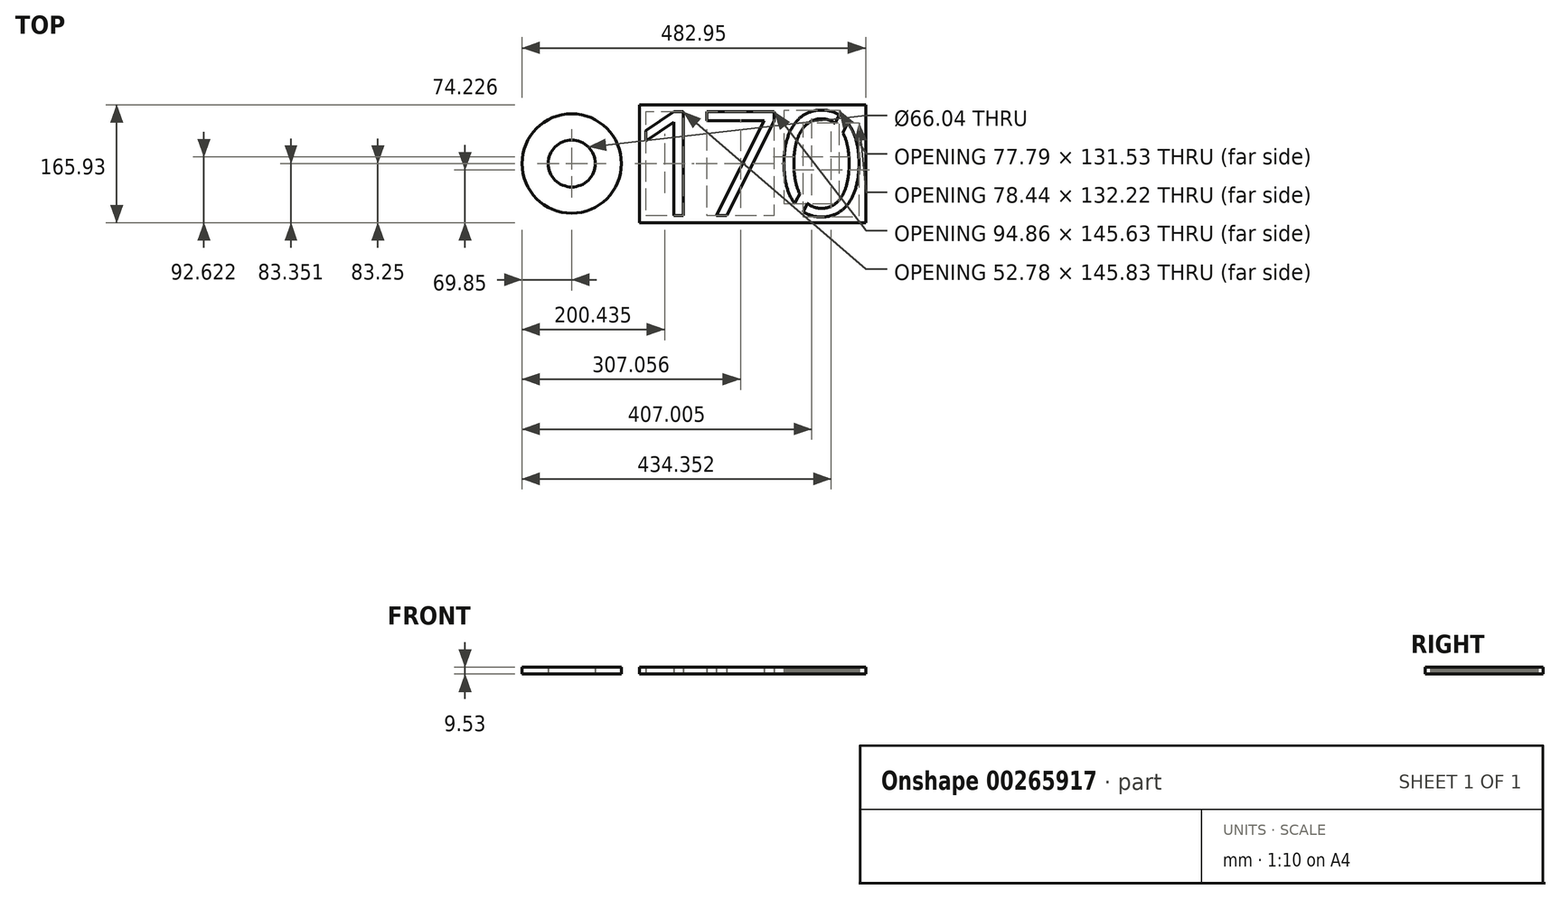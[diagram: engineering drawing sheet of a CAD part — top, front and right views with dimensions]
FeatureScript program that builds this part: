
annotation { "Feature Type Name" : "Feature", "Feature Type Description" : "" }
export const myFeature = defineFeature(function(context is Context, id is Id, definition is map)
    precondition{}
    {
        {
            var Q0;
            Q0=qCreatedBy(makeId("Top.planeOp"),FACE);
            var sketch = newSketch(context, id + "F0", { "sketchPlane" : qUnion([Q0])});
            skCircle(sketch, "E0", {"center": v(0, 0) * mm, "radius": 33.02 * mm});
            skCircle(sketch, "E1", {"center": v(0, 0) * mm, "radius": 69.85 * mm});
            skLineSegment(sketch, "E2", {"start": v(143.65, 58.18) * mm, "end": v(143.25, 58.18) * mm});
            skLineSegment(sketch, "E3", {"start": v(143.25, 58.18) * mm, "end": v(104.2, 31.34) * mm});
            skLineSegment(sketch, "E4", {"start": v(104.2, 31.34) * mm, "end": v(104.2, 46.07) * mm});
            skLineSegment(sketch, "E5", {"start": v(104.2, 46.07) * mm, "end": v(143.45, 73.02) * mm});
            skLineSegment(sketch, "E6", {"start": v(143.45, 73.02) * mm, "end": v(156.98, 73.02) * mm});
            skLineSegment(sketch, "E7", {"start": v(156.98, 73.02) * mm, "end": v(156.98, -72.81) * mm});
            skLineSegment(sketch, "E8", {"start": v(156.98, -72.81) * mm, "end": v(143.65, -72.81) * mm});
            skLineSegment(sketch, "E9", {"start": v(143.65, -72.81) * mm, "end": v(143.65, 58.18) * mm});
            skLineSegment(sketch, "E10", {"start": v(270.81, 60.1) * mm, "end": v(270.81, 60.5) * mm});
            skLineSegment(sketch, "E11", {"start": v(270.81, 60.5) * mm, "end": v(189.77, 60.5) * mm});
            skLineSegment(sketch, "E12", {"start": v(189.77, 60.5) * mm, "end": v(189.77, 72.81) * mm});
            skLineSegment(sketch, "E13", {"start": v(189.77, 72.81) * mm, "end": v(284.64, 72.81) * mm});
            skLineSegment(sketch, "E14", {"start": v(284.64, 72.81) * mm, "end": v(284.64, 59.9) * mm});
            skLineSegment(sketch, "E15", {"start": v(284.64, 59.9) * mm, "end": v(217.93, -72.81) * mm});
            skLineSegment(sketch, "E16", {"start": v(217.93, -72.81) * mm, "end": v(203.3, -72.81) * mm});
            skLineSegment(sketch, "E17", {"start": v(203.3, -72.81) * mm, "end": v(270.81, 60.1) * mm});
            skLineSegment(sketch, "E18", {"start": v(298.32, -4.21) * mm, "end": v(298.4, -6.3) * mm});
            skLineSegment(sketch, "E19", {"start": v(298.4, -6.3) * mm, "end": v(298.5, -8.38) * mm});
            skLineSegment(sketch, "E20", {"start": v(298.5, -8.38) * mm, "end": v(298.62, -10.42) * mm});
            skLineSegment(sketch, "E21", {"start": v(298.62, -10.42) * mm, "end": v(298.78, -12.44) * mm});
            skLineSegment(sketch, "E22", {"start": v(298.78, -12.44) * mm, "end": v(298.96, -14.43) * mm});
            skLineSegment(sketch, "E23", {"start": v(298.96, -14.43) * mm, "end": v(299.17, -16.4) * mm});
            skLineSegment(sketch, "E24", {"start": v(299.17, -16.4) * mm, "end": v(299.41, -18.33) * mm});
            skLineSegment(sketch, "E25", {"start": v(299.41, -18.33) * mm, "end": v(299.68, -20.24) * mm});
            skLineSegment(sketch, "E26", {"start": v(299.68, -20.24) * mm, "end": v(299.97, -22.12) * mm});
            skLineSegment(sketch, "E27", {"start": v(299.97, -22.12) * mm, "end": v(300.3, -23.98) * mm});
            skLineSegment(sketch, "E28", {"start": v(300.3, -23.98) * mm, "end": v(300.65, -25.8) * mm});
            skLineSegment(sketch, "E29", {"start": v(300.65, -25.8) * mm, "end": v(301.02, -27.6) * mm});
            skLineSegment(sketch, "E30", {"start": v(301.02, -27.6) * mm, "end": v(301.42, -29.37) * mm});
            skLineSegment(sketch, "E31", {"start": v(301.42, -29.37) * mm, "end": v(301.85, -31.11) * mm});
            skLineSegment(sketch, "E32", {"start": v(301.85, -31.11) * mm, "end": v(302.3, -32.82) * mm});
            skLineSegment(sketch, "E33", {"start": v(302.3, -32.82) * mm, "end": v(302.8, -34.5) * mm});
            skLineSegment(sketch, "E34", {"start": v(302.8, -34.5) * mm, "end": v(303.3, -36.16) * mm});
            skLineSegment(sketch, "E35", {"start": v(303.3, -36.16) * mm, "end": v(303.84, -37.78) * mm});
            skLineSegment(sketch, "E36", {"start": v(303.84, -37.78) * mm, "end": v(304.4, -39.37) * mm});
            skLineSegment(sketch, "E37", {"start": v(304.4, -39.37) * mm, "end": v(304.98, -40.93) * mm});
            skLineSegment(sketch, "E38", {"start": v(304.98, -40.93) * mm, "end": v(305.6, -42.46) * mm});
            skLineSegment(sketch, "E39", {"start": v(305.6, -42.46) * mm, "end": v(306.23, -43.96) * mm});
            skLineSegment(sketch, "E40", {"start": v(306.23, -43.96) * mm, "end": v(306.9, -45.43) * mm});
            skLineSegment(sketch, "E41", {"start": v(306.9, -45.43) * mm, "end": v(307.59, -46.87) * mm});
            skLineSegment(sketch, "E42", {"start": v(307.59, -46.87) * mm, "end": v(308.3, -48.27) * mm});
            skLineSegment(sketch, "E43", {"start": v(308.3, -48.27) * mm, "end": v(309.04, -49.64) * mm});
            skLineSegment(sketch, "E44", {"start": v(309.04, -49.64) * mm, "end": v(309.8, -50.98) * mm});
            skLineSegment(sketch, "E45", {"start": v(309.8, -50.98) * mm, "end": v(310.59, -52.29) * mm});
            skLineSegment(sketch, "E46", {"start": v(310.59, -52.29) * mm, "end": v(311.4, -53.56) * mm});
            skLineSegment(sketch, "E47", {"start": v(311.4, -53.56) * mm, "end": v(312.24, -54.8) * mm});
            skLineSegment(sketch, "E48", {"start": v(312.24, -54.8) * mm, "end": v(313.1, -56) * mm});
            skLineSegment(sketch, "E49", {"start": v(313.1, -56) * mm, "end": v(313.4, -56.4) * mm});
            skLineSegment(sketch, "E50", {"start": v(313.4, -56.4) * mm, "end": v(315.27, -52.65) * mm});
            skLineSegment(sketch, "E51", {"start": v(315.27, -52.65) * mm, "end": v(320.43, -42.4) * mm});
            skLineSegment(sketch, "E52", {"start": v(320.43, -42.4) * mm, "end": v(320.04, -41.6) * mm});
            skLineSegment(sketch, "E53", {"start": v(320.04, -41.6) * mm, "end": v(319.5, -40.44) * mm});
            skLineSegment(sketch, "E54", {"start": v(319.5, -40.44) * mm, "end": v(318.98, -39.26) * mm});
            skLineSegment(sketch, "E55", {"start": v(318.98, -39.26) * mm, "end": v(318.47, -38.06) * mm});
            skLineSegment(sketch, "E56", {"start": v(318.47, -38.06) * mm, "end": v(317.99, -36.82) * mm});
            skLineSegment(sketch, "E57", {"start": v(317.99, -36.82) * mm, "end": v(317.52, -35.56) * mm});
            skLineSegment(sketch, "E58", {"start": v(317.52, -35.56) * mm, "end": v(317.08, -34.28) * mm});
            skLineSegment(sketch, "E59", {"start": v(317.08, -34.28) * mm, "end": v(316.65, -32.97) * mm});
            skLineSegment(sketch, "E60", {"start": v(316.65, -32.97) * mm, "end": v(316.24, -31.63) * mm});
            skLineSegment(sketch, "E61", {"start": v(316.24, -31.63) * mm, "end": v(315.85, -30.27) * mm});
            skLineSegment(sketch, "E62", {"start": v(315.85, -30.27) * mm, "end": v(315.48, -28.88) * mm});
            skLineSegment(sketch, "E63", {"start": v(315.48, -28.88) * mm, "end": v(315.13, -27.46) * mm});
            skLineSegment(sketch, "E64", {"start": v(315.13, -27.46) * mm, "end": v(314.8, -26.03) * mm});
            skLineSegment(sketch, "E65", {"start": v(314.8, -26.03) * mm, "end": v(314.48, -24.56) * mm});
            skLineSegment(sketch, "E66", {"start": v(314.48, -24.56) * mm, "end": v(314.2, -23.08) * mm});
            skLineSegment(sketch, "E67", {"start": v(314.2, -23.08) * mm, "end": v(313.92, -21.57) * mm});
            skLineSegment(sketch, "E68", {"start": v(313.92, -21.57) * mm, "end": v(313.66, -20.03) * mm});
            skLineSegment(sketch, "E69", {"start": v(313.66, -20.03) * mm, "end": v(313.43, -18.47) * mm});
            skLineSegment(sketch, "E70", {"start": v(313.43, -18.47) * mm, "end": v(313.22, -16.9) * mm});
            skLineSegment(sketch, "E71", {"start": v(313.22, -16.9) * mm, "end": v(313.02, -15.29) * mm});
            skLineSegment(sketch, "E72", {"start": v(313.02, -15.29) * mm, "end": v(312.85, -13.66) * mm});
            skLineSegment(sketch, "E73", {"start": v(312.85, -13.66) * mm, "end": v(312.7, -12.01) * mm});
            skLineSegment(sketch, "E74", {"start": v(312.7, -12.01) * mm, "end": v(312.56, -10.34) * mm});
            skLineSegment(sketch, "E75", {"start": v(312.56, -10.34) * mm, "end": v(312.45, -8.64) * mm});
            skLineSegment(sketch, "E76", {"start": v(312.45, -8.64) * mm, "end": v(312.35, -6.93) * mm});
            skLineSegment(sketch, "E77", {"start": v(312.35, -6.93) * mm, "end": v(312.28, -5.19) * mm});
            skLineSegment(sketch, "E78", {"start": v(312.28, -5.19) * mm, "end": v(312.23, -3.43) * mm});
            skLineSegment(sketch, "E79", {"start": v(312.23, -3.43) * mm, "end": v(312.2, -1.65) * mm});
            skLineSegment(sketch, "E80", {"start": v(312.2, -1.65) * mm, "end": v(312.19, 0.15) * mm});
            skLineSegment(sketch, "E81", {"start": v(312.19, 0.15) * mm, "end": v(312.2, 1.92) * mm});
            skLineSegment(sketch, "E82", {"start": v(312.2, 1.92) * mm, "end": v(312.23, 3.67) * mm});
            skLineSegment(sketch, "E83", {"start": v(312.23, 3.67) * mm, "end": v(312.28, 5.4) * mm});
            skLineSegment(sketch, "E84", {"start": v(312.28, 5.4) * mm, "end": v(312.36, 7.1) * mm});
            skLineSegment(sketch, "E85", {"start": v(312.36, 7.1) * mm, "end": v(312.45, 8.8) * mm});
            skLineSegment(sketch, "E86", {"start": v(312.45, 8.8) * mm, "end": v(312.57, 10.47) * mm});
            skLineSegment(sketch, "E87", {"start": v(312.57, 10.47) * mm, "end": v(312.7, 12.12) * mm});
            skLineSegment(sketch, "E88", {"start": v(312.7, 12.12) * mm, "end": v(312.86, 13.74) * mm});
            skLineSegment(sketch, "E89", {"start": v(312.86, 13.74) * mm, "end": v(313.04, 15.35) * mm});
            skLineSegment(sketch, "E90", {"start": v(313.04, 15.35) * mm, "end": v(313.24, 16.93) * mm});
            skLineSegment(sketch, "E91", {"start": v(313.24, 16.93) * mm, "end": v(313.45, 18.5) * mm});
            skLineSegment(sketch, "E92", {"start": v(313.45, 18.5) * mm, "end": v(313.7, 20.04) * mm});
            skLineSegment(sketch, "E93", {"start": v(313.7, 20.04) * mm, "end": v(313.95, 21.55) * mm});
            skLineSegment(sketch, "E94", {"start": v(313.95, 21.55) * mm, "end": v(314.23, 23.05) * mm});
            skLineSegment(sketch, "E95", {"start": v(314.23, 23.05) * mm, "end": v(314.52, 24.52) * mm});
            skLineSegment(sketch, "E96", {"start": v(314.52, 24.52) * mm, "end": v(314.84, 25.97) * mm});
            skLineSegment(sketch, "E97", {"start": v(314.84, 25.97) * mm, "end": v(315.18, 27.4) * mm});
            skLineSegment(sketch, "E98", {"start": v(315.18, 27.4) * mm, "end": v(315.53, 28.8) * mm});
            skLineSegment(sketch, "E99", {"start": v(315.53, 28.8) * mm, "end": v(315.9, 30.17) * mm});
            skLineSegment(sketch, "E100", {"start": v(315.9, 30.17) * mm, "end": v(316.3, 31.52) * mm});
            skLineSegment(sketch, "E101", {"start": v(316.3, 31.52) * mm, "end": v(316.72, 32.85) * mm});
            skLineSegment(sketch, "E102", {"start": v(316.72, 32.85) * mm, "end": v(317.15, 34.16) * mm});
            skLineSegment(sketch, "E103", {"start": v(317.15, 34.16) * mm, "end": v(317.6, 35.44) * mm});
            skLineSegment(sketch, "E104", {"start": v(317.6, 35.44) * mm, "end": v(318.07, 36.69) * mm});
            skLineSegment(sketch, "E105", {"start": v(318.07, 36.69) * mm, "end": v(318.56, 37.92) * mm});
            skLineSegment(sketch, "E106", {"start": v(318.56, 37.92) * mm, "end": v(319.07, 39.12) * mm});
            skLineSegment(sketch, "E107", {"start": v(319.07, 39.12) * mm, "end": v(319.6, 40.3) * mm});
            skLineSegment(sketch, "E108", {"start": v(319.6, 40.3) * mm, "end": v(320.14, 41.44) * mm});
            skLineSegment(sketch, "E109", {"start": v(320.14, 41.44) * mm, "end": v(320.7, 42.56) * mm});
            skLineSegment(sketch, "E110", {"start": v(320.7, 42.56) * mm, "end": v(321.28, 43.66) * mm});
            skLineSegment(sketch, "E111", {"start": v(321.28, 43.66) * mm, "end": v(321.88, 44.73) * mm});
            skLineSegment(sketch, "E112", {"start": v(321.88, 44.73) * mm, "end": v(322.5, 45.77) * mm});
            skLineSegment(sketch, "E113", {"start": v(322.5, 45.77) * mm, "end": v(323.13, 46.78) * mm});
            skLineSegment(sketch, "E114", {"start": v(323.13, 46.78) * mm, "end": v(323.78, 47.76) * mm});
            skLineSegment(sketch, "E115", {"start": v(323.78, 47.76) * mm, "end": v(324.45, 48.72) * mm});
            skLineSegment(sketch, "E116", {"start": v(324.45, 48.72) * mm, "end": v(325.14, 49.65) * mm});
            skLineSegment(sketch, "E117", {"start": v(325.14, 49.65) * mm, "end": v(325.84, 50.55) * mm});
            skLineSegment(sketch, "E118", {"start": v(325.84, 50.55) * mm, "end": v(326.57, 51.42) * mm});
            skLineSegment(sketch, "E119", {"start": v(326.57, 51.42) * mm, "end": v(327.3, 52.26) * mm});
            skLineSegment(sketch, "E120", {"start": v(327.3, 52.26) * mm, "end": v(328.06, 53.07) * mm});
            skLineSegment(sketch, "E121", {"start": v(328.06, 53.07) * mm, "end": v(328.83, 53.85) * mm});
            skLineSegment(sketch, "E122", {"start": v(328.83, 53.85) * mm, "end": v(329.62, 54.6) * mm});
            skLineSegment(sketch, "E123", {"start": v(329.62, 54.6) * mm, "end": v(330.43, 55.32) * mm});
            skLineSegment(sketch, "E124", {"start": v(330.43, 55.32) * mm, "end": v(331.25, 56) * mm});
            skLineSegment(sketch, "E125", {"start": v(331.25, 56) * mm, "end": v(332.1, 56.67) * mm});
            skLineSegment(sketch, "E126", {"start": v(332.1, 56.67) * mm, "end": v(332.95, 57.3) * mm});
            skLineSegment(sketch, "E127", {"start": v(332.95, 57.3) * mm, "end": v(333.82, 57.89) * mm});
            skLineSegment(sketch, "E128", {"start": v(333.82, 57.89) * mm, "end": v(334.71, 58.45) * mm});
            skLineSegment(sketch, "E129", {"start": v(334.71, 58.45) * mm, "end": v(335.62, 58.98) * mm});
            skLineSegment(sketch, "E130", {"start": v(335.62, 58.98) * mm, "end": v(336.54, 59.48) * mm});
            skLineSegment(sketch, "E131", {"start": v(336.54, 59.48) * mm, "end": v(337.47, 59.95) * mm});
            skLineSegment(sketch, "E132", {"start": v(337.47, 59.95) * mm, "end": v(338.43, 60.38) * mm});
            skLineSegment(sketch, "E133", {"start": v(338.43, 60.38) * mm, "end": v(339.4, 60.78) * mm});
            skLineSegment(sketch, "E134", {"start": v(339.4, 60.78) * mm, "end": v(340.38, 61.15) * mm});
            skLineSegment(sketch, "E135", {"start": v(340.38, 61.15) * mm, "end": v(341.38, 61.48) * mm});
            skLineSegment(sketch, "E136", {"start": v(341.38, 61.48) * mm, "end": v(342.4, 61.78) * mm});
            skLineSegment(sketch, "E137", {"start": v(342.4, 61.78) * mm, "end": v(343.42, 62.05) * mm});
            skLineSegment(sketch, "E138", {"start": v(343.42, 62.05) * mm, "end": v(344.46, 62.28) * mm});
            skLineSegment(sketch, "E139", {"start": v(344.46, 62.28) * mm, "end": v(345.52, 62.47) * mm});
            skLineSegment(sketch, "E140", {"start": v(345.52, 62.47) * mm, "end": v(346.6, 62.64) * mm});
            skLineSegment(sketch, "E141", {"start": v(346.6, 62.64) * mm, "end": v(347.69, 62.76) * mm});
            skLineSegment(sketch, "E142", {"start": v(347.69, 62.76) * mm, "end": v(348.8, 62.85) * mm});
            skLineSegment(sketch, "E143", {"start": v(348.8, 62.85) * mm, "end": v(349.91, 62.9) * mm});
            skLineSegment(sketch, "E144", {"start": v(349.91, 62.9) * mm, "end": v(351.04, 62.92) * mm});
            skLineSegment(sketch, "E145", {"start": v(351.04, 62.92) * mm, "end": v(352.18, 62.9) * mm});
            skLineSegment(sketch, "E146", {"start": v(352.18, 62.9) * mm, "end": v(353.3, 62.85) * mm});
            skLineSegment(sketch, "E147", {"start": v(353.3, 62.85) * mm, "end": v(354.41, 62.76) * mm});
            skLineSegment(sketch, "E148", {"start": v(354.41, 62.76) * mm, "end": v(355.5, 62.64) * mm});
            skLineSegment(sketch, "E149", {"start": v(355.5, 62.64) * mm, "end": v(356.58, 62.48) * mm});
            skLineSegment(sketch, "E150", {"start": v(356.58, 62.48) * mm, "end": v(357.64, 62.28) * mm});
            skLineSegment(sketch, "E151", {"start": v(357.64, 62.28) * mm, "end": v(358.7, 62.05) * mm});
            skLineSegment(sketch, "E152", {"start": v(358.7, 62.05) * mm, "end": v(359.72, 61.8) * mm});
            skLineSegment(sketch, "E153", {"start": v(359.72, 61.8) * mm, "end": v(360.74, 61.5) * mm});
            skLineSegment(sketch, "E154", {"start": v(360.74, 61.5) * mm, "end": v(361.74, 61.16) * mm});
            skLineSegment(sketch, "E155", {"start": v(361.74, 61.16) * mm, "end": v(362.73, 60.8) * mm});
            skLineSegment(sketch, "E156", {"start": v(362.73, 60.8) * mm, "end": v(363.7, 60.4) * mm});
            skLineSegment(sketch, "E157", {"start": v(363.7, 60.4) * mm, "end": v(364.65, 59.97) * mm});
            skLineSegment(sketch, "E158", {"start": v(364.65, 59.97) * mm, "end": v(365.59, 59.5) * mm});
            skLineSegment(sketch, "E159", {"start": v(365.59, 59.5) * mm, "end": v(366.51, 59) * mm});
            skLineSegment(sketch, "E160", {"start": v(366.51, 59) * mm, "end": v(367.42, 58.48) * mm});
            skLineSegment(sketch, "E161", {"start": v(367.42, 58.48) * mm, "end": v(368.3, 57.92) * mm});
            skLineSegment(sketch, "E162", {"start": v(368.3, 57.92) * mm, "end": v(369.18, 57.32) * mm});
            skLineSegment(sketch, "E163", {"start": v(369.18, 57.32) * mm, "end": v(370.04, 56.7) * mm});
            skLineSegment(sketch, "E164", {"start": v(370.04, 56.7) * mm, "end": v(370.2, 56.57) * mm});
            skLineSegment(sketch, "E165", {"start": v(370.2, 56.57) * mm, "end": v(372, 60.15) * mm});
            skLineSegment(sketch, "E166", {"start": v(372, 60.15) * mm, "end": v(376.05, 68.18) * mm});
            skLineSegment(sketch, "E167", {"start": v(376.05, 68.18) * mm, "end": v(375.58, 68.47) * mm});
            skLineSegment(sketch, "E168", {"start": v(375.58, 68.47) * mm, "end": v(374.4, 69.18) * mm});
            skLineSegment(sketch, "E169", {"start": v(374.4, 69.18) * mm, "end": v(373.2, 69.85) * mm});
            skLineSegment(sketch, "E170", {"start": v(373.2, 69.85) * mm, "end": v(371.97, 70.48) * mm});
            skLineSegment(sketch, "E171", {"start": v(371.97, 70.48) * mm, "end": v(370.72, 71.07) * mm});
            skLineSegment(sketch, "E172", {"start": v(370.72, 71.07) * mm, "end": v(369.45, 71.62) * mm});
            skLineSegment(sketch, "E173", {"start": v(369.45, 71.62) * mm, "end": v(368.16, 72.13) * mm});
            skLineSegment(sketch, "E174", {"start": v(368.16, 72.13) * mm, "end": v(366.85, 72.6) * mm});
            skLineSegment(sketch, "E175", {"start": v(366.85, 72.6) * mm, "end": v(365.51, 73.04) * mm});
            skLineSegment(sketch, "E176", {"start": v(365.51, 73.04) * mm, "end": v(364.16, 73.43) * mm});
            skLineSegment(sketch, "E177", {"start": v(364.16, 73.43) * mm, "end": v(362.78, 73.79) * mm});
            skLineSegment(sketch, "E178", {"start": v(362.78, 73.79) * mm, "end": v(361.38, 74.1) * mm});
            skLineSegment(sketch, "E179", {"start": v(361.38, 74.1) * mm, "end": v(359.97, 74.37) * mm});
            skLineSegment(sketch, "E180", {"start": v(359.97, 74.37) * mm, "end": v(358.53, 74.6) * mm});
            skLineSegment(sketch, "E181", {"start": v(358.53, 74.6) * mm, "end": v(357.07, 74.8) * mm});
            skLineSegment(sketch, "E182", {"start": v(357.07, 74.8) * mm, "end": v(355.6, 74.94) * mm});
            skLineSegment(sketch, "E183", {"start": v(355.6, 74.94) * mm, "end": v(354.1, 75.05) * mm});
            skLineSegment(sketch, "E184", {"start": v(354.1, 75.05) * mm, "end": v(352.58, 75.11) * mm});
            skLineSegment(sketch, "E185", {"start": v(352.58, 75.11) * mm, "end": v(351.04, 75.13) * mm});
            skLineSegment(sketch, "E186", {"start": v(351.04, 75.13) * mm, "end": v(349.51, 75.11) * mm});
            skLineSegment(sketch, "E187", {"start": v(349.51, 75.11) * mm, "end": v(348, 75.05) * mm});
            skLineSegment(sketch, "E188", {"start": v(348, 75.05) * mm, "end": v(346.5, 74.94) * mm});
            skLineSegment(sketch, "E189", {"start": v(346.5, 74.94) * mm, "end": v(345.03, 74.8) * mm});
            skLineSegment(sketch, "E190", {"start": v(345.03, 74.8) * mm, "end": v(343.57, 74.6) * mm});
            skLineSegment(sketch, "E191", {"start": v(343.57, 74.6) * mm, "end": v(342.14, 74.37) * mm});
            skLineSegment(sketch, "E192", {"start": v(342.14, 74.37) * mm, "end": v(340.72, 74.1) * mm});
            skLineSegment(sketch, "E193", {"start": v(340.72, 74.1) * mm, "end": v(339.33, 73.78) * mm});
            skLineSegment(sketch, "E194", {"start": v(339.33, 73.78) * mm, "end": v(337.95, 73.43) * mm});
            skLineSegment(sketch, "E195", {"start": v(337.95, 73.43) * mm, "end": v(336.6, 73.03) * mm});
            skLineSegment(sketch, "E196", {"start": v(336.6, 73.03) * mm, "end": v(335.27, 72.6) * mm});
            skLineSegment(sketch, "E197", {"start": v(335.27, 72.6) * mm, "end": v(333.96, 72.12) * mm});
            skLineSegment(sketch, "E198", {"start": v(333.96, 72.12) * mm, "end": v(332.66, 71.6) * mm});
            skLineSegment(sketch, "E199", {"start": v(332.66, 71.6) * mm, "end": v(331.4, 71.06) * mm});
            skLineSegment(sketch, "E200", {"start": v(331.4, 71.06) * mm, "end": v(330.14, 70.46) * mm});
            skLineSegment(sketch, "E201", {"start": v(330.14, 70.46) * mm, "end": v(328.92, 69.83) * mm});
            skLineSegment(sketch, "E202", {"start": v(328.92, 69.83) * mm, "end": v(327.71, 69.16) * mm});
            skLineSegment(sketch, "E203", {"start": v(327.71, 69.16) * mm, "end": v(326.53, 68.46) * mm});
            skLineSegment(sketch, "E204", {"start": v(326.53, 68.46) * mm, "end": v(325.36, 67.71) * mm});
            skLineSegment(sketch, "E205", {"start": v(325.36, 67.71) * mm, "end": v(324.22, 66.93) * mm});
            skLineSegment(sketch, "E206", {"start": v(324.22, 66.93) * mm, "end": v(323.1, 66.1) * mm});
            skLineSegment(sketch, "E207", {"start": v(323.1, 66.1) * mm, "end": v(322, 65.25) * mm});
            skLineSegment(sketch, "E208", {"start": v(322, 65.25) * mm, "end": v(320.94, 64.36) * mm});
            skLineSegment(sketch, "E209", {"start": v(320.94, 64.36) * mm, "end": v(319.88, 63.43) * mm});
            skLineSegment(sketch, "E210", {"start": v(319.88, 63.43) * mm, "end": v(318.86, 62.47) * mm});
            skLineSegment(sketch, "E211", {"start": v(318.86, 62.47) * mm, "end": v(317.85, 61.47) * mm});
            skLineSegment(sketch, "E212", {"start": v(317.85, 61.47) * mm, "end": v(316.87, 60.43) * mm});
            skLineSegment(sketch, "E213", {"start": v(316.87, 60.43) * mm, "end": v(315.91, 59.36) * mm});
            skLineSegment(sketch, "E214", {"start": v(315.91, 59.36) * mm, "end": v(314.98, 58.26) * mm});
            skLineSegment(sketch, "E215", {"start": v(314.98, 58.26) * mm, "end": v(314.07, 57.12) * mm});
            skLineSegment(sketch, "E216", {"start": v(314.07, 57.12) * mm, "end": v(313.18, 55.94) * mm});
            skLineSegment(sketch, "E217", {"start": v(313.18, 55.94) * mm, "end": v(312.31, 54.74) * mm});
            skLineSegment(sketch, "E218", {"start": v(312.31, 54.74) * mm, "end": v(311.48, 53.5) * mm});
            skLineSegment(sketch, "E219", {"start": v(311.48, 53.5) * mm, "end": v(310.66, 52.22) * mm});
            skLineSegment(sketch, "E220", {"start": v(310.66, 52.22) * mm, "end": v(309.87, 50.91) * mm});
            skLineSegment(sketch, "E221", {"start": v(309.87, 50.91) * mm, "end": v(309.1, 49.58) * mm});
            skLineSegment(sketch, "E222", {"start": v(309.1, 49.58) * mm, "end": v(308.36, 48.2) * mm});
            skLineSegment(sketch, "E223", {"start": v(308.36, 48.2) * mm, "end": v(307.65, 46.8) * mm});
            skLineSegment(sketch, "E224", {"start": v(307.65, 46.8) * mm, "end": v(306.95, 45.36) * mm});
            skLineSegment(sketch, "E225", {"start": v(306.95, 45.36) * mm, "end": v(306.29, 43.9) * mm});
            skLineSegment(sketch, "E226", {"start": v(306.29, 43.9) * mm, "end": v(305.65, 42.4) * mm});
            skLineSegment(sketch, "E227", {"start": v(305.65, 42.4) * mm, "end": v(305.03, 40.87) * mm});
            skLineSegment(sketch, "E228", {"start": v(305.03, 40.87) * mm, "end": v(304.44, 39.31) * mm});
            skLineSegment(sketch, "E229", {"start": v(304.44, 39.31) * mm, "end": v(303.88, 37.72) * mm});
            skLineSegment(sketch, "E230", {"start": v(303.88, 37.72) * mm, "end": v(303.34, 36.1) * mm});
            skLineSegment(sketch, "E231", {"start": v(303.34, 36.1) * mm, "end": v(302.83, 34.45) * mm});
            skLineSegment(sketch, "E232", {"start": v(302.83, 34.45) * mm, "end": v(302.34, 32.78) * mm});
            skLineSegment(sketch, "E233", {"start": v(302.34, 32.78) * mm, "end": v(301.88, 31.07) * mm});
            skLineSegment(sketch, "E234", {"start": v(301.88, 31.07) * mm, "end": v(301.45, 29.33) * mm});
            skLineSegment(sketch, "E235", {"start": v(301.45, 29.33) * mm, "end": v(301.04, 27.57) * mm});
            skLineSegment(sketch, "E236", {"start": v(301.04, 27.57) * mm, "end": v(300.67, 25.78) * mm});
            skLineSegment(sketch, "E237", {"start": v(300.67, 25.78) * mm, "end": v(300.31, 23.96) * mm});
            skLineSegment(sketch, "E238", {"start": v(300.31, 23.96) * mm, "end": v(299.99, 22.1) * mm});
            skLineSegment(sketch, "E239", {"start": v(299.99, 22.1) * mm, "end": v(299.7, 20.23) * mm});
            skLineSegment(sketch, "E240", {"start": v(299.7, 20.23) * mm, "end": v(299.42, 18.33) * mm});
            skLineSegment(sketch, "E241", {"start": v(299.42, 18.33) * mm, "end": v(299.18, 16.4) * mm});
            skLineSegment(sketch, "E242", {"start": v(299.18, 16.4) * mm, "end": v(298.97, 14.45) * mm});
            skLineSegment(sketch, "E243", {"start": v(298.97, 14.45) * mm, "end": v(298.78, 12.47) * mm});
            skLineSegment(sketch, "E244", {"start": v(298.78, 12.47) * mm, "end": v(298.62, 10.46) * mm});
            skLineSegment(sketch, "E245", {"start": v(298.62, 10.46) * mm, "end": v(298.5, 8.43) * mm});
            skLineSegment(sketch, "E246", {"start": v(298.5, 8.43) * mm, "end": v(298.4, 6.37) * mm});
            skLineSegment(sketch, "E247", {"start": v(298.4, 6.37) * mm, "end": v(298.32, 4.29) * mm});
            skLineSegment(sketch, "E248", {"start": v(298.32, 4.29) * mm, "end": v(298.28, 2.18) * mm});
            skLineSegment(sketch, "E249", {"start": v(298.28, 2.18) * mm, "end": v(298.26, 0.05) * mm});
            skLineSegment(sketch, "E250", {"start": v(298.26, 0.05) * mm, "end": v(298.28, -2.1) * mm});
            skLineSegment(sketch, "E251", {"start": v(298.28, -2.1) * mm, "end": v(298.32, -4.21) * mm});
            skLineSegment(sketch, "E252", {"start": v(403.67, 4.39) * mm, "end": v(403.6, 6.47) * mm});
            skLineSegment(sketch, "E253", {"start": v(403.6, 6.47) * mm, "end": v(403.5, 8.53) * mm});
            skLineSegment(sketch, "E254", {"start": v(403.5, 8.53) * mm, "end": v(403.37, 10.56) * mm});
            skLineSegment(sketch, "E255", {"start": v(403.37, 10.56) * mm, "end": v(403.2, 12.56) * mm});
            skLineSegment(sketch, "E256", {"start": v(403.2, 12.56) * mm, "end": v(403.03, 14.55) * mm});
            skLineSegment(sketch, "E257", {"start": v(403.03, 14.55) * mm, "end": v(402.81, 16.5) * mm});
            skLineSegment(sketch, "E258", {"start": v(402.81, 16.5) * mm, "end": v(402.57, 18.43) * mm});
            skLineSegment(sketch, "E259", {"start": v(402.57, 18.43) * mm, "end": v(402.3, 20.33) * mm});
            skLineSegment(sketch, "E260", {"start": v(402.3, 20.33) * mm, "end": v(402.01, 22.2) * mm});
            skLineSegment(sketch, "E261", {"start": v(402.01, 22.2) * mm, "end": v(401.69, 24.05) * mm});
            skLineSegment(sketch, "E262", {"start": v(401.69, 24.05) * mm, "end": v(401.34, 25.87) * mm});
            skLineSegment(sketch, "E263", {"start": v(401.34, 25.87) * mm, "end": v(400.96, 27.66) * mm});
            skLineSegment(sketch, "E264", {"start": v(400.96, 27.66) * mm, "end": v(400.56, 29.42) * mm});
            skLineSegment(sketch, "E265", {"start": v(400.56, 29.42) * mm, "end": v(400.13, 31.15) * mm});
            skLineSegment(sketch, "E266", {"start": v(400.13, 31.15) * mm, "end": v(399.68, 32.86) * mm});
            skLineSegment(sketch, "E267", {"start": v(399.68, 32.86) * mm, "end": v(399.2, 34.54) * mm});
            skLineSegment(sketch, "E268", {"start": v(399.2, 34.54) * mm, "end": v(398.69, 36.18) * mm});
            skLineSegment(sketch, "E269", {"start": v(398.69, 36.18) * mm, "end": v(398.15, 37.8) * mm});
            skLineSegment(sketch, "E270", {"start": v(398.15, 37.8) * mm, "end": v(397.6, 39.39) * mm});
            skLineSegment(sketch, "E271", {"start": v(397.6, 39.39) * mm, "end": v(397, 40.94) * mm});
            skLineSegment(sketch, "E272", {"start": v(397, 40.94) * mm, "end": v(396.4, 42.47) * mm});
            skLineSegment(sketch, "E273", {"start": v(396.4, 42.47) * mm, "end": v(395.76, 43.97) * mm});
            skLineSegment(sketch, "E274", {"start": v(395.76, 43.97) * mm, "end": v(395.1, 45.43) * mm});
            skLineSegment(sketch, "E275", {"start": v(395.1, 45.43) * mm, "end": v(394.4, 46.86) * mm});
            skLineSegment(sketch, "E276", {"start": v(394.4, 46.86) * mm, "end": v(393.7, 48.27) * mm});
            skLineSegment(sketch, "E277", {"start": v(393.7, 48.27) * mm, "end": v(392.96, 49.64) * mm});
            skLineSegment(sketch, "E278", {"start": v(392.96, 49.64) * mm, "end": v(392.2, 50.97) * mm});
            skLineSegment(sketch, "E279", {"start": v(392.2, 50.97) * mm, "end": v(391.4, 52.28) * mm});
            skLineSegment(sketch, "E280", {"start": v(391.4, 52.28) * mm, "end": v(390.6, 53.55) * mm});
            skLineSegment(sketch, "E281", {"start": v(390.6, 53.55) * mm, "end": v(389.76, 54.79) * mm});
            skLineSegment(sketch, "E282", {"start": v(389.76, 54.79) * mm, "end": v(388.9, 56) * mm});
            skLineSegment(sketch, "E283", {"start": v(388.9, 56) * mm, "end": v(388.07, 57.09) * mm});
            skLineSegment(sketch, "E284", {"start": v(388.07, 57.09) * mm, "end": v(386.06, 53.08) * mm});
            skLineSegment(sketch, "E285", {"start": v(386.06, 53.08) * mm, "end": v(381.1, 43.23) * mm});
            skLineSegment(sketch, "E286", {"start": v(381.1, 43.23) * mm, "end": v(381.42, 42.63) * mm});
            skLineSegment(sketch, "E287", {"start": v(381.42, 42.63) * mm, "end": v(381.98, 41.5) * mm});
            skLineSegment(sketch, "E288", {"start": v(381.98, 41.5) * mm, "end": v(382.53, 40.36) * mm});
            skLineSegment(sketch, "E289", {"start": v(382.53, 40.36) * mm, "end": v(383.05, 39.18) * mm});
            skLineSegment(sketch, "E290", {"start": v(383.05, 39.18) * mm, "end": v(383.56, 37.98) * mm});
            skLineSegment(sketch, "E291", {"start": v(383.56, 37.98) * mm, "end": v(384.04, 36.75) * mm});
            skLineSegment(sketch, "E292", {"start": v(384.04, 36.75) * mm, "end": v(384.51, 35.5) * mm});
            skLineSegment(sketch, "E293", {"start": v(384.51, 35.5) * mm, "end": v(384.96, 34.22) * mm});
            skLineSegment(sketch, "E294", {"start": v(384.96, 34.22) * mm, "end": v(385.4, 32.91) * mm});
            skLineSegment(sketch, "E295", {"start": v(385.4, 32.91) * mm, "end": v(385.8, 31.58) * mm});
            skLineSegment(sketch, "E296", {"start": v(385.8, 31.58) * mm, "end": v(386.2, 30.23) * mm});
            skLineSegment(sketch, "E297", {"start": v(386.2, 30.23) * mm, "end": v(386.57, 28.84) * mm});
            skLineSegment(sketch, "E298", {"start": v(386.57, 28.84) * mm, "end": v(386.93, 27.44) * mm});
            skLineSegment(sketch, "E299", {"start": v(386.93, 27.44) * mm, "end": v(387.26, 26.01) * mm});
            skLineSegment(sketch, "E300", {"start": v(387.26, 26.01) * mm, "end": v(387.58, 24.56) * mm});
            skLineSegment(sketch, "E301", {"start": v(387.58, 24.56) * mm, "end": v(387.87, 23.08) * mm});
            skLineSegment(sketch, "E302", {"start": v(387.87, 23.08) * mm, "end": v(388.15, 21.58) * mm});
            skLineSegment(sketch, "E303", {"start": v(388.15, 21.58) * mm, "end": v(388.4, 20.06) * mm});
            skLineSegment(sketch, "E304", {"start": v(388.4, 20.06) * mm, "end": v(388.64, 18.5) * mm});
            skLineSegment(sketch, "E305", {"start": v(388.64, 18.5) * mm, "end": v(388.86, 16.94) * mm});
            skLineSegment(sketch, "E306", {"start": v(388.86, 16.94) * mm, "end": v(389.05, 15.35) * mm});
            skLineSegment(sketch, "E307", {"start": v(389.05, 15.35) * mm, "end": v(389.23, 13.73) * mm});
            skLineSegment(sketch, "E308", {"start": v(389.23, 13.73) * mm, "end": v(389.39, 12.1) * mm});
            skLineSegment(sketch, "E309", {"start": v(389.39, 12.1) * mm, "end": v(389.52, 10.44) * mm});
            skLineSegment(sketch, "E310", {"start": v(389.52, 10.44) * mm, "end": v(389.64, 8.76) * mm});
            skLineSegment(sketch, "E311", {"start": v(389.64, 8.76) * mm, "end": v(389.73, 7.06) * mm});
            skLineSegment(sketch, "E312", {"start": v(389.73, 7.06) * mm, "end": v(389.8, 5.34) * mm});
            skLineSegment(sketch, "E313", {"start": v(389.8, 5.34) * mm, "end": v(389.85, 3.6) * mm});
            skLineSegment(sketch, "E314", {"start": v(389.85, 3.6) * mm, "end": v(389.89, 1.83) * mm});
            skLineSegment(sketch, "E315", {"start": v(389.89, 1.83) * mm, "end": v(389.9, 0.05) * mm});
            skLineSegment(sketch, "E316", {"start": v(389.9, 0.05) * mm, "end": v(389.89, -1.75) * mm});
            skLineSegment(sketch, "E317", {"start": v(389.89, -1.75) * mm, "end": v(389.86, -3.52) * mm});
            skLineSegment(sketch, "E318", {"start": v(389.86, -3.52) * mm, "end": v(389.8, -5.28) * mm});
            skLineSegment(sketch, "E319", {"start": v(389.8, -5.28) * mm, "end": v(389.73, -7.01) * mm});
            skLineSegment(sketch, "E320", {"start": v(389.73, -7.01) * mm, "end": v(389.64, -8.72) * mm});
            skLineSegment(sketch, "E321", {"start": v(389.64, -8.72) * mm, "end": v(389.53, -10.41) * mm});
            skLineSegment(sketch, "E322", {"start": v(389.53, -10.41) * mm, "end": v(389.4, -12.08) * mm});
            skLineSegment(sketch, "E323", {"start": v(389.4, -12.08) * mm, "end": v(389.24, -13.73) * mm});
            skLineSegment(sketch, "E324", {"start": v(389.24, -13.73) * mm, "end": v(389.06, -15.35) * mm});
            skLineSegment(sketch, "E325", {"start": v(389.06, -15.35) * mm, "end": v(388.87, -16.95) * mm});
            skLineSegment(sketch, "E326", {"start": v(388.87, -16.95) * mm, "end": v(388.66, -18.53) * mm});
            skLineSegment(sketch, "E327", {"start": v(388.66, -18.53) * mm, "end": v(388.42, -20.09) * mm});
            skLineSegment(sketch, "E328", {"start": v(388.42, -20.09) * mm, "end": v(388.17, -21.62) * mm});
            skLineSegment(sketch, "E329", {"start": v(388.17, -21.62) * mm, "end": v(387.9, -23.13) * mm});
            skLineSegment(sketch, "E330", {"start": v(387.9, -23.13) * mm, "end": v(387.6, -24.6) * mm});
            skLineSegment(sketch, "E331", {"start": v(387.6, -24.6) * mm, "end": v(387.29, -26.07) * mm});
            skLineSegment(sketch, "E332", {"start": v(387.29, -26.07) * mm, "end": v(386.96, -27.5) * mm});
            skLineSegment(sketch, "E333", {"start": v(386.96, -27.5) * mm, "end": v(386.6, -28.91) * mm});
            skLineSegment(sketch, "E334", {"start": v(386.6, -28.91) * mm, "end": v(386.24, -30.3) * mm});
            skLineSegment(sketch, "E335", {"start": v(386.24, -30.3) * mm, "end": v(385.85, -31.66) * mm});
            skLineSegment(sketch, "E336", {"start": v(385.85, -31.66) * mm, "end": v(385.44, -33) * mm});
            skLineSegment(sketch, "E337", {"start": v(385.44, -33) * mm, "end": v(385, -34.3) * mm});
            skLineSegment(sketch, "E338", {"start": v(385, -34.3) * mm, "end": v(384.56, -35.6) * mm});
            skLineSegment(sketch, "E339", {"start": v(384.56, -35.6) * mm, "end": v(384.1, -36.85) * mm});
            skLineSegment(sketch, "E340", {"start": v(384.1, -36.85) * mm, "end": v(383.61, -38.08) * mm});
            skLineSegment(sketch, "E341", {"start": v(383.61, -38.08) * mm, "end": v(383.1, -39.28) * mm});
            skLineSegment(sketch, "E342", {"start": v(383.1, -39.28) * mm, "end": v(382.59, -40.46) * mm});
            skLineSegment(sketch, "E343", {"start": v(382.59, -40.46) * mm, "end": v(382.05, -41.61) * mm});
            skLineSegment(sketch, "E344", {"start": v(382.05, -41.61) * mm, "end": v(381.49, -42.74) * mm});
            skLineSegment(sketch, "E345", {"start": v(381.49, -42.74) * mm, "end": v(380.91, -43.83) * mm});
            skLineSegment(sketch, "E346", {"start": v(380.91, -43.83) * mm, "end": v(380.32, -44.9) * mm});
            skLineSegment(sketch, "E347", {"start": v(380.32, -44.9) * mm, "end": v(379.7, -45.94) * mm});
            skLineSegment(sketch, "E348", {"start": v(379.7, -45.94) * mm, "end": v(379.07, -46.96) * mm});
            skLineSegment(sketch, "E349", {"start": v(379.07, -46.96) * mm, "end": v(378.42, -47.94) * mm});
            skLineSegment(sketch, "E350", {"start": v(378.42, -47.94) * mm, "end": v(377.76, -48.9) * mm});
            skLineSegment(sketch, "E351", {"start": v(377.76, -48.9) * mm, "end": v(377.07, -49.82) * mm});
            skLineSegment(sketch, "E352", {"start": v(377.07, -49.82) * mm, "end": v(376.37, -50.72) * mm});
            skLineSegment(sketch, "E353", {"start": v(376.37, -50.72) * mm, "end": v(375.65, -51.59) * mm});
            skLineSegment(sketch, "E354", {"start": v(375.65, -51.59) * mm, "end": v(374.91, -52.42) * mm});
            skLineSegment(sketch, "E355", {"start": v(374.91, -52.42) * mm, "end": v(374.16, -53.23) * mm});
            skLineSegment(sketch, "E356", {"start": v(374.16, -53.23) * mm, "end": v(373.39, -54) * mm});
            skLineSegment(sketch, "E357", {"start": v(373.39, -54) * mm, "end": v(372.6, -54.76) * mm});
            skLineSegment(sketch, "E358", {"start": v(372.6, -54.76) * mm, "end": v(371.79, -55.47) * mm});
            skLineSegment(sketch, "E359", {"start": v(371.79, -55.47) * mm, "end": v(370.97, -56.16) * mm});
            skLineSegment(sketch, "E360", {"start": v(370.97, -56.16) * mm, "end": v(370.13, -56.81) * mm});
            skLineSegment(sketch, "E361", {"start": v(370.13, -56.81) * mm, "end": v(369.27, -57.44) * mm});
            skLineSegment(sketch, "E362", {"start": v(369.27, -57.44) * mm, "end": v(368.4, -58.03) * mm});
            skLineSegment(sketch, "E363", {"start": v(368.4, -58.03) * mm, "end": v(367.5, -58.6) * mm});
            skLineSegment(sketch, "E364", {"start": v(367.5, -58.6) * mm, "end": v(366.6, -59.12) * mm});
            skLineSegment(sketch, "E365", {"start": v(366.6, -59.12) * mm, "end": v(365.67, -59.61) * mm});
            skLineSegment(sketch, "E366", {"start": v(365.67, -59.61) * mm, "end": v(364.73, -60.08) * mm});
            skLineSegment(sketch, "E367", {"start": v(364.73, -60.08) * mm, "end": v(363.77, -60.5) * mm});
            skLineSegment(sketch, "E368", {"start": v(363.77, -60.5) * mm, "end": v(362.8, -60.9) * mm});
            skLineSegment(sketch, "E369", {"start": v(362.8, -60.9) * mm, "end": v(361.8, -61.27) * mm});
            skLineSegment(sketch, "E370", {"start": v(361.8, -61.27) * mm, "end": v(360.8, -61.6) * mm});
            skLineSegment(sketch, "E371", {"start": v(360.8, -61.6) * mm, "end": v(359.78, -61.9) * mm});
            skLineSegment(sketch, "E372", {"start": v(359.78, -61.9) * mm, "end": v(358.74, -62.16) * mm});
            skLineSegment(sketch, "E373", {"start": v(358.74, -62.16) * mm, "end": v(357.7, -62.39) * mm});
            skLineSegment(sketch, "E374", {"start": v(357.7, -62.39) * mm, "end": v(356.62, -62.58) * mm});
            skLineSegment(sketch, "E375", {"start": v(356.62, -62.58) * mm, "end": v(355.54, -62.74) * mm});
            skLineSegment(sketch, "E376", {"start": v(355.54, -62.74) * mm, "end": v(354.44, -62.86) * mm});
            skLineSegment(sketch, "E377", {"start": v(354.44, -62.86) * mm, "end": v(353.32, -62.95) * mm});
            skLineSegment(sketch, "E378", {"start": v(353.32, -62.95) * mm, "end": v(352.19, -63) * mm});
            skLineSegment(sketch, "E379", {"start": v(352.19, -63) * mm, "end": v(351.04, -63.02) * mm});
            skLineSegment(sketch, "E380", {"start": v(351.04, -63.02) * mm, "end": v(349.9, -63) * mm});
            skLineSegment(sketch, "E381", {"start": v(349.9, -63) * mm, "end": v(348.77, -62.95) * mm});
            skLineSegment(sketch, "E382", {"start": v(348.77, -62.95) * mm, "end": v(347.65, -62.86) * mm});
            skLineSegment(sketch, "E383", {"start": v(347.65, -62.86) * mm, "end": v(346.55, -62.74) * mm});
            skLineSegment(sketch, "E384", {"start": v(346.55, -62.74) * mm, "end": v(345.46, -62.58) * mm});
            skLineSegment(sketch, "E385", {"start": v(345.46, -62.58) * mm, "end": v(344.4, -62.39) * mm});
            skLineSegment(sketch, "E386", {"start": v(344.4, -62.39) * mm, "end": v(343.34, -62.16) * mm});
            skLineSegment(sketch, "E387", {"start": v(343.34, -62.16) * mm, "end": v(342.3, -61.9) * mm});
            skLineSegment(sketch, "E388", {"start": v(342.3, -61.9) * mm, "end": v(341.28, -61.6) * mm});
            skLineSegment(sketch, "E389", {"start": v(341.28, -61.6) * mm, "end": v(340.28, -61.27) * mm});
            skLineSegment(sketch, "E390", {"start": v(340.28, -61.27) * mm, "end": v(339.29, -60.9) * mm});
            skLineSegment(sketch, "E391", {"start": v(339.29, -60.9) * mm, "end": v(338.31, -60.5) * mm});
            skLineSegment(sketch, "E392", {"start": v(338.31, -60.5) * mm, "end": v(337.36, -60.08) * mm});
            skLineSegment(sketch, "E393", {"start": v(337.36, -60.08) * mm, "end": v(336.42, -59.61) * mm});
            skLineSegment(sketch, "E394", {"start": v(336.42, -59.61) * mm, "end": v(335.5, -59.12) * mm});
            skLineSegment(sketch, "E395", {"start": v(335.5, -59.12) * mm, "end": v(334.58, -58.59) * mm});
            skLineSegment(sketch, "E396", {"start": v(334.58, -58.59) * mm, "end": v(333.7, -58.03) * mm});
            skLineSegment(sketch, "E397", {"start": v(333.7, -58.03) * mm, "end": v(332.82, -57.44) * mm});
            skLineSegment(sketch, "E398", {"start": v(332.82, -57.44) * mm, "end": v(331.96, -56.81) * mm});
            skLineSegment(sketch, "E399", {"start": v(331.96, -56.81) * mm, "end": v(331.12, -56.16) * mm});
            skLineSegment(sketch, "E400", {"start": v(331.12, -56.16) * mm, "end": v(331.11, -56.15) * mm});
            skLineSegment(sketch, "E401", {"start": v(331.11, -56.15) * mm, "end": v(329.32, -59.72) * mm});
            skLineSegment(sketch, "E402", {"start": v(329.32, -59.72) * mm, "end": v(325.28, -67.75) * mm});
            skLineSegment(sketch, "E403", {"start": v(325.28, -67.75) * mm, "end": v(326.44, -68.49) * mm});
            skLineSegment(sketch, "E404", {"start": v(326.44, -68.49) * mm, "end": v(327.62, -69.2) * mm});
            skLineSegment(sketch, "E405", {"start": v(327.62, -69.2) * mm, "end": v(328.83, -69.86) * mm});
            skLineSegment(sketch, "E406", {"start": v(328.83, -69.86) * mm, "end": v(330.06, -70.49) * mm});
            skLineSegment(sketch, "E407", {"start": v(330.06, -70.49) * mm, "end": v(331.31, -71.08) * mm});
            skLineSegment(sketch, "E408", {"start": v(331.31, -71.08) * mm, "end": v(332.59, -71.63) * mm});
            skLineSegment(sketch, "E409", {"start": v(332.59, -71.63) * mm, "end": v(333.88, -72.14) * mm});
            skLineSegment(sketch, "E410", {"start": v(333.88, -72.14) * mm, "end": v(335.2, -72.61) * mm});
            skLineSegment(sketch, "E411", {"start": v(335.2, -72.61) * mm, "end": v(336.53, -73.05) * mm});
            skLineSegment(sketch, "E412", {"start": v(336.53, -73.05) * mm, "end": v(337.9, -73.44) * mm});
            skLineSegment(sketch, "E413", {"start": v(337.9, -73.44) * mm, "end": v(339.27, -73.8) * mm});
            skLineSegment(sketch, "E414", {"start": v(339.27, -73.8) * mm, "end": v(340.67, -74.1) * mm});
            skLineSegment(sketch, "E415", {"start": v(340.67, -74.1) * mm, "end": v(342.1, -74.38) * mm});
            skLineSegment(sketch, "E416", {"start": v(342.1, -74.38) * mm, "end": v(343.53, -74.6) * mm});
            skLineSegment(sketch, "E417", {"start": v(343.53, -74.6) * mm, "end": v(345, -74.8) * mm});
            skLineSegment(sketch, "E418", {"start": v(345, -74.8) * mm, "end": v(346.48, -74.94) * mm});
            skLineSegment(sketch, "E419", {"start": v(346.48, -74.94) * mm, "end": v(347.98, -75.05) * mm});
            skLineSegment(sketch, "E420", {"start": v(347.98, -75.05) * mm, "end": v(349.5, -75.11) * mm});
            skLineSegment(sketch, "E421", {"start": v(349.5, -75.11) * mm, "end": v(351.04, -75.13) * mm});
            skLineSegment(sketch, "E422", {"start": v(351.04, -75.13) * mm, "end": v(352.58, -75.11) * mm});
            skLineSegment(sketch, "E423", {"start": v(352.58, -75.11) * mm, "end": v(354.1, -75.05) * mm});
            skLineSegment(sketch, "E424", {"start": v(354.1, -75.05) * mm, "end": v(355.6, -74.94) * mm});
            skLineSegment(sketch, "E425", {"start": v(355.6, -74.94) * mm, "end": v(357.09, -74.8) * mm});
            skLineSegment(sketch, "E426", {"start": v(357.09, -74.8) * mm, "end": v(358.55, -74.6) * mm});
            skLineSegment(sketch, "E427", {"start": v(358.55, -74.6) * mm, "end": v(360, -74.37) * mm});
            skLineSegment(sketch, "E428", {"start": v(360, -74.37) * mm, "end": v(361.41, -74.1) * mm});
            skLineSegment(sketch, "E429", {"start": v(361.41, -74.1) * mm, "end": v(362.81, -73.79) * mm});
            skLineSegment(sketch, "E430", {"start": v(362.81, -73.79) * mm, "end": v(364.19, -73.43) * mm});
            skLineSegment(sketch, "E431", {"start": v(364.19, -73.43) * mm, "end": v(365.55, -73.04) * mm});
            skLineSegment(sketch, "E432", {"start": v(365.55, -73.04) * mm, "end": v(366.88, -72.6) * mm});
            skLineSegment(sketch, "E433", {"start": v(366.88, -72.6) * mm, "end": v(368.2, -72.13) * mm});
            skLineSegment(sketch, "E434", {"start": v(368.2, -72.13) * mm, "end": v(369.49, -71.62) * mm});
            skLineSegment(sketch, "E435", {"start": v(369.49, -71.62) * mm, "end": v(370.76, -71.06) * mm});
            skLineSegment(sketch, "E436", {"start": v(370.76, -71.06) * mm, "end": v(372.01, -70.47) * mm});
            skLineSegment(sketch, "E437", {"start": v(372.01, -70.47) * mm, "end": v(373.24, -69.84) * mm});
            skLineSegment(sketch, "E438", {"start": v(373.24, -69.84) * mm, "end": v(374.44, -69.17) * mm});
            skLineSegment(sketch, "E439", {"start": v(374.44, -69.17) * mm, "end": v(375.63, -68.47) * mm});
            skLineSegment(sketch, "E440", {"start": v(375.63, -68.47) * mm, "end": v(376.8, -67.72) * mm});
            skLineSegment(sketch, "E441", {"start": v(376.8, -67.72) * mm, "end": v(377.93, -66.94) * mm});
            skLineSegment(sketch, "E442", {"start": v(377.93, -66.94) * mm, "end": v(379.05, -66.12) * mm});
            skLineSegment(sketch, "E443", {"start": v(379.05, -66.12) * mm, "end": v(380.14, -65.27) * mm});
            skLineSegment(sketch, "E444", {"start": v(380.14, -65.27) * mm, "end": v(381.21, -64.38) * mm});
            skLineSegment(sketch, "E445", {"start": v(381.21, -64.38) * mm, "end": v(382.26, -63.45) * mm});
            skLineSegment(sketch, "E446", {"start": v(382.26, -63.45) * mm, "end": v(383.28, -62.48) * mm});
            skLineSegment(sketch, "E447", {"start": v(383.28, -62.48) * mm, "end": v(384.28, -61.48) * mm});
            skLineSegment(sketch, "E448", {"start": v(384.28, -61.48) * mm, "end": v(385.26, -60.45) * mm});
            skLineSegment(sketch, "E449", {"start": v(385.26, -60.45) * mm, "end": v(386.22, -59.38) * mm});
            skLineSegment(sketch, "E450", {"start": v(386.22, -59.38) * mm, "end": v(387.15, -58.27) * mm});
            skLineSegment(sketch, "E451", {"start": v(387.15, -58.27) * mm, "end": v(388.05, -57.13) * mm});
            skLineSegment(sketch, "E452", {"start": v(388.05, -57.13) * mm, "end": v(388.94, -55.96) * mm});
            skLineSegment(sketch, "E453", {"start": v(388.94, -55.96) * mm, "end": v(389.8, -54.75) * mm});
            skLineSegment(sketch, "E454", {"start": v(389.8, -54.75) * mm, "end": v(390.63, -53.5) * mm});
            skLineSegment(sketch, "E455", {"start": v(390.63, -53.5) * mm, "end": v(391.44, -52.23) * mm});
            skLineSegment(sketch, "E456", {"start": v(391.44, -52.23) * mm, "end": v(392.23, -50.92) * mm});
            skLineSegment(sketch, "E457", {"start": v(392.23, -50.92) * mm, "end": v(392.99, -49.58) * mm});
            skLineSegment(sketch, "E458", {"start": v(392.99, -49.58) * mm, "end": v(393.72, -48.2) * mm});
            skLineSegment(sketch, "E459", {"start": v(393.72, -48.2) * mm, "end": v(394.44, -46.8) * mm});
            skLineSegment(sketch, "E460", {"start": v(394.44, -46.8) * mm, "end": v(395.12, -45.36) * mm});
            skLineSegment(sketch, "E461", {"start": v(395.12, -45.36) * mm, "end": v(395.78, -43.9) * mm});
            skLineSegment(sketch, "E462", {"start": v(395.78, -43.9) * mm, "end": v(396.42, -42.4) * mm});
            skLineSegment(sketch, "E463", {"start": v(396.42, -42.4) * mm, "end": v(397.03, -40.86) * mm});
            skLineSegment(sketch, "E464", {"start": v(397.03, -40.86) * mm, "end": v(397.61, -39.3) * mm});
            skLineSegment(sketch, "E465", {"start": v(397.61, -39.3) * mm, "end": v(398.17, -37.7) * mm});
            skLineSegment(sketch, "E466", {"start": v(398.17, -37.7) * mm, "end": v(398.7, -36.08) * mm});
            skLineSegment(sketch, "E467", {"start": v(398.7, -36.08) * mm, "end": v(399.21, -34.42) * mm});
            skLineSegment(sketch, "E468", {"start": v(399.21, -34.42) * mm, "end": v(399.7, -32.74) * mm});
            skLineSegment(sketch, "E469", {"start": v(399.7, -32.74) * mm, "end": v(400.15, -31.03) * mm});
            skLineSegment(sketch, "E470", {"start": v(400.15, -31.03) * mm, "end": v(400.57, -29.28) * mm});
            skLineSegment(sketch, "E471", {"start": v(400.57, -29.28) * mm, "end": v(400.98, -27.51) * mm});
            skLineSegment(sketch, "E472", {"start": v(400.98, -27.51) * mm, "end": v(401.35, -25.71) * mm});
            skLineSegment(sketch, "E473", {"start": v(401.35, -25.71) * mm, "end": v(401.7, -23.89) * mm});
            skLineSegment(sketch, "E474", {"start": v(401.7, -23.89) * mm, "end": v(402.02, -22.03) * mm});
            skLineSegment(sketch, "E475", {"start": v(402.02, -22.03) * mm, "end": v(402.31, -20.15) * mm});
            skLineSegment(sketch, "E476", {"start": v(402.31, -20.15) * mm, "end": v(402.58, -18.23) * mm});
            skLineSegment(sketch, "E477", {"start": v(402.58, -18.23) * mm, "end": v(402.82, -16.3) * mm});
            skLineSegment(sketch, "E478", {"start": v(402.82, -16.3) * mm, "end": v(403.03, -14.33) * mm});
            skLineSegment(sketch, "E479", {"start": v(403.03, -14.33) * mm, "end": v(403.21, -12.34) * mm});
            skLineSegment(sketch, "E480", {"start": v(403.21, -12.34) * mm, "end": v(403.37, -10.32) * mm});
            skLineSegment(sketch, "E481", {"start": v(403.37, -10.32) * mm, "end": v(403.5, -8.28) * mm});
            skLineSegment(sketch, "E482", {"start": v(403.5, -8.28) * mm, "end": v(403.6, -6.2) * mm});
            skLineSegment(sketch, "E483", {"start": v(403.6, -6.2) * mm, "end": v(403.67, -4.11) * mm});
            skLineSegment(sketch, "E484", {"start": v(403.67, -4.11) * mm, "end": v(403.7, -2) * mm});
            skLineSegment(sketch, "E485", {"start": v(403.7, -2) * mm, "end": v(403.72, 0.15) * mm});
            skLineSegment(sketch, "E486", {"start": v(403.72, 0.15) * mm, "end": v(403.7, 2.28) * mm});
            skLineSegment(sketch, "E487", {"start": v(403.7, 2.28) * mm, "end": v(403.67, 4.39) * mm});
            skLineSegment(sketch, "E488.bottom", {"start": v(95.21, 82.68) * mm, "end": v(413.1, 82.68) * mm});
            skLineSegment(sketch, "E488.top", {"start": v(95.21, -83.25) * mm, "end": v(413.1, -83.25) * mm});
            skLineSegment(sketch, "E488.left", {"start": v(95.21, 82.68) * mm, "end": v(95.21, -83.25) * mm});
            skLineSegment(sketch, "E488.right", {"start": v(413.1, 82.68) * mm, "end": v(413.1, -83.25) * mm});
            skSolve(sketch);
        }
        {
            var Q0;
            Q0=makeQuery(id+"F0.imprint","IMPRINT",FACE,{"disambiguationData":[TD([[makeQuery(id+"F0.imprint","IMPRINT",EDGE,{"derivedFrom":sQuery(id+"F0.wireOp",EDGE,"E0")}),-1.0]])]});
            var Q1;
            Q1=makeQuery(id+"F0.imprint","IMPRINT",FACE,{"disambiguationData":[TD([[makeQuery(id+"F0.imprint","IMPRINT",EDGE,{"derivedFrom":sQuery(id+"F0.wireOp",EDGE,"E2")}),1.0]])]});
            extrude(context, id + "F1", {"entities" : qUnion([Q0, Q1]), "depth" : 9.52 * mm});
        }
    });
